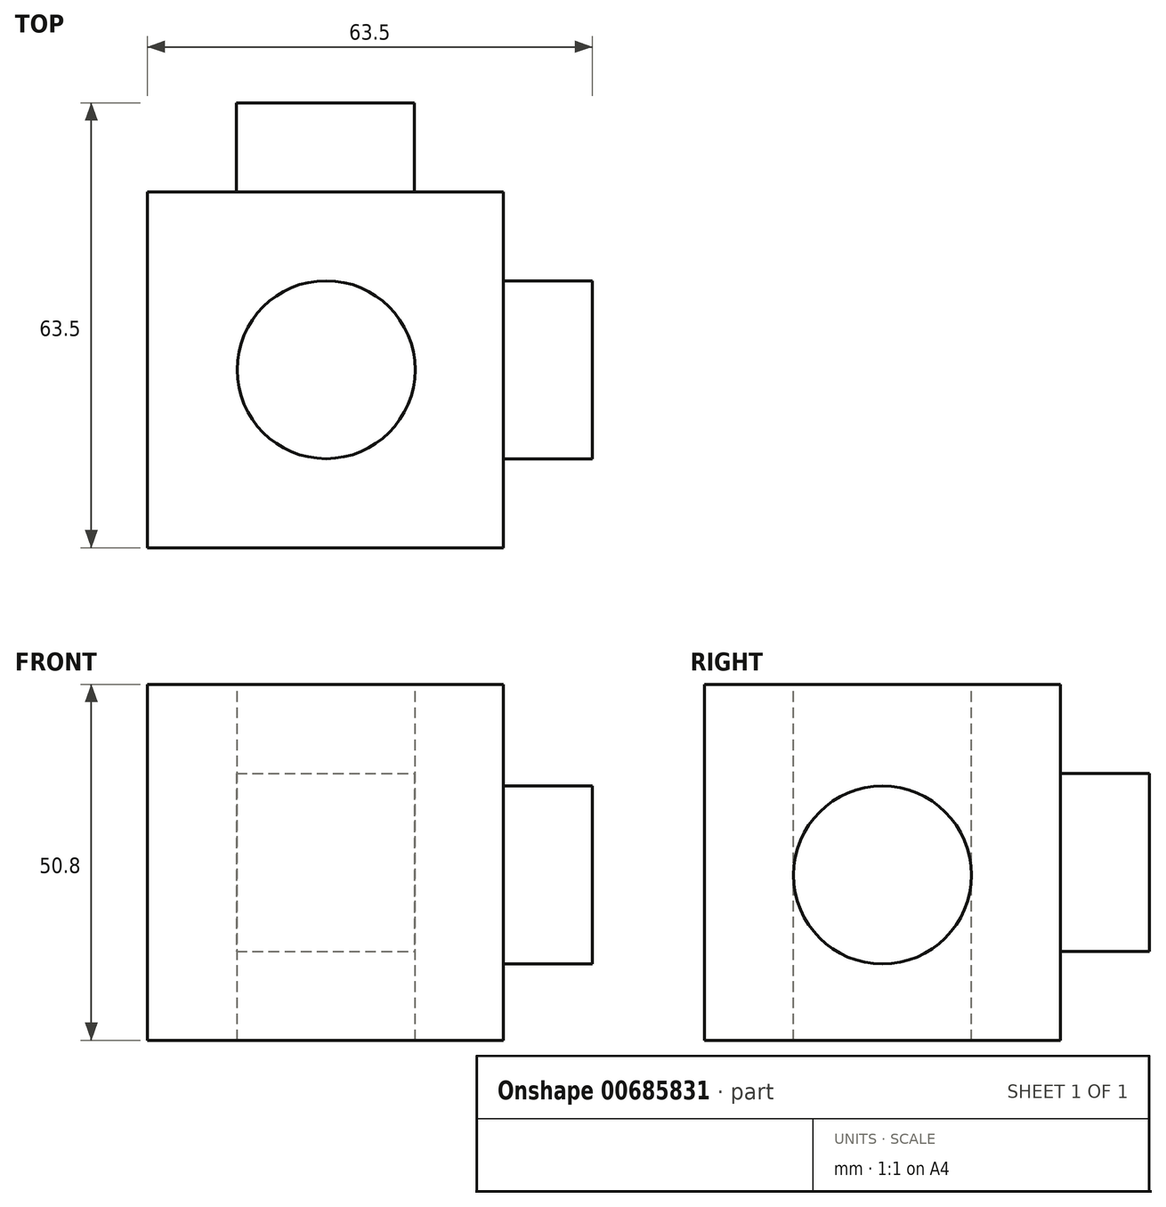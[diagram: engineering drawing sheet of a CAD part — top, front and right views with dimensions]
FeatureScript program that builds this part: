
annotation { "Feature Type Name" : "Feature", "Feature Type Description" : "" }
export const myFeature = defineFeature(function(context is Context, id is Id, definition is map)
    precondition{}
    {
        {
            var Q0;
            Q0=qCreatedBy(makeId("Front.planeOp"),FACE);
            var sketch = newSketch(context, id + "F0", { "sketchPlane" : qUnion([Q0])});
            skLineSegment(sketch, "E0.bottom", {"start": v(-25.5, 27.22) * mm, "end": v(25.3, 27.22) * mm});
            skLineSegment(sketch, "E0.top", {"start": v(-25.5, -23.58) * mm, "end": v(25.3, -23.58) * mm});
            skLineSegment(sketch, "E0.left", {"start": v(-25.5, 27.22) * mm, "end": v(-25.5, -23.58) * mm});
            skLineSegment(sketch, "E0.right", {"start": v(25.3, 27.22) * mm, "end": v(25.3, -23.58) * mm});
            skSolve(sketch);
        }
        {
            var Q0;
            Q0=makeQuery(id+"F0.imprint","IMPRINT",FACE,{"disambiguationData":[TD([[makeQuery(id+"F0.imprint","IMPRINT",EDGE,{"derivedFrom":sQuery(id+"F0.wireOp",EDGE,"E0.bottom")}),-1.0]])]});
            extrude(context, id + "F1", {"entities" : qUnion([Q0]), "depth" : 50.8 * mm, "offsetDistance" : 25.4 * mm});
        }
        {
            var Q0;
            Q0=qCreatedBy(makeId("Front.planeOp"),FACE);
            var sketch = newSketch(context, id + "F2", { "sketchPlane" : qUnion([Q0])});
            skLineSegment(sketch, "E1.bottom", {"start": v(-12.8, 14.52) * mm, "end": v(12.6, 14.52) * mm});
            skLineSegment(sketch, "E1.top", {"start": v(-12.8, -10.88) * mm, "end": v(12.6, -10.88) * mm});
            skLineSegment(sketch, "E1.left", {"start": v(-12.8, 14.52) * mm, "end": v(-12.8, -10.88) * mm});
            skLineSegment(sketch, "E1.right", {"start": v(12.6, 14.52) * mm, "end": v(12.6, -10.88) * mm});
            skSolve(sketch);
        }
        {
            var Q0;
            Q0=makeQuery(id+"F2.imprint","IMPRINT",FACE,{"disambiguationData":[TD([[makeQuery(id+"F2.imprint","IMPRINT",EDGE,{"derivedFrom":sQuery(id+"F2.wireOp",EDGE,"E1.bottom")}),-1.0]])]});
            extrude(context, id + "F3", {"entities" : qUnion([Q0]), "operationType" : NewBodyOperationType.ADD, "oppositeDirection" : true, "depth" : 12.7 * mm, "offsetDistance" : 25.4 * mm});
        }
        {
            var Q0;
            Q0=makeQuery(id+"F1.opExtrude","SWEPT_FACE",FACE,{"disambiguationData":[OSD([sQuery(id+"F0.wireOp",EDGE,"E0.right")])]});
            var sketch = newSketch(context, id + "F4", { "sketchPlane" : qUnion([Q0])});
            skCircle(sketch, "E2", {"center": v(-25.4, 0) * mm, "radius": 12.7 * mm});
            skPoint(sketch, "E2.centerSnap0", {"position": v(-25.4, 27.22) * mm});
            skSolve(sketch);
        }
        {
            var Q0;
            Q0=makeQuery(id+"F4.imprint","IMPRINT",FACE,{"disambiguationData":[TD([[makeQuery(id+"F4.imprint","IMPRINT",EDGE,{"derivedFrom":sQuery(id+"F4.wireOp",EDGE,"E2")}),1.0]])]});
            extrude(context, id + "F5", {"entities" : qUnion([Q0]), "operationType" : NewBodyOperationType.ADD, "depth" : 12.7 * mm, "offsetDistance" : 25.4 * mm});
        }
        {
            var Q0;
            Q0=makeQuery(id+"F1.opExtrude","SWEPT_FACE",FACE,{"disambiguationData":[OSD([sQuery(id+"F0.wireOp",EDGE,"E0.bottom")])]});
            var sketch = newSketch(context, id + "F6", { "sketchPlane" : qUnion([Q0])});
            skCircle(sketch, "E3", {"center": v(0, -25.4) * mm, "radius": 12.7 * mm});
            skPoint(sketch, "E3.centerSnap0", {"position": v(25.3, -25.4) * mm});
            skSolve(sketch);
        }
        {
            var Q0;
            Q0=makeQuery(id+"F6.imprint","IMPRINT",FACE,{"disambiguationData":[TD([[makeQuery(id+"F6.imprint","IMPRINT",EDGE,{"derivedFrom":sQuery(id+"F6.wireOp",EDGE,"E3")}),1.0]])]});
            extrude(context, id + "F7", {"entities" : qUnion([Q0]), "operationType" : NewBodyOperationType.REMOVE, "oppositeDirection" : true, "depth" : 50.8 * mm, "offsetDistance" : 25.4 * mm});
        }
    });
